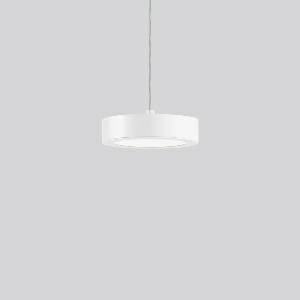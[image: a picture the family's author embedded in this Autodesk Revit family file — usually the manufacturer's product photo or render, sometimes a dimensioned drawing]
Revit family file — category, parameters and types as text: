
# Revit family: toledo_flat_round_p_901685_002_1_76_fe41
name_source: partatom
category: Lighting Fixtures
units: mm (PartAtom-declared; Revit-internal decimal feet)

## family parameters
Cut with Voids When Loaded = No
Host = Face
Light Source = No
Part Type = Normal
Room Calculation Point = No
Round Connector Dimension = Use Diameter
Shared = No

## types (1)
- TOLEDO FLAT round P (1 x LED Modul 840, 1800 lm, 4000)
    Apparent Load = 17 VA
    CIE Flux Codes = 48 79 96 100 100
    Color Rendering = 80
    Color Temperature = 4000
    Default Elevation = 1800 mm  [stored 5.90551 ft]
    Description = Series: TOLEDO FLAT
Flat cylindrical pendant luminaire. Cylinder housing sheet steel, powder-coated. Housing: die cast aluminium and sheet steel, powder-coated. Bezel ring: die-cast aluminium, powder-coated. Canopy: sheet steel, powder-coated. Lightguide and diffuser made of non-yellowing plastic (PMMA) opal matt. Suitable for pendant. Transparent suspension cable 2 m, can be shortened. Mounting rings for retrofitting a fabric lampshade available as accessory. 
Colour: white
Diameter: 257 mm
Height: 88.8 mm
Suspension length: 2000 mm
Lamp: LED
Socket: without socket
Colour temperature: 4000K
Colour rendering index (CRI): 80
System power: 17 W
Rated luminous flux: 1800 lm
Luminous efficiency: 106 lm/W
Control gear: Converter, dimmable, DALI
Protection class: I
Type of protection: IP 20
    Height = 89 mm
    Lamp = 1 x LED Modul 840
    Lamp Light Flux = 1800 lm
    Lamp count = 1
    Length = 257 mm
    Lifetime = 50000 h
    Luminous efficacy = 106 lm/W
    Manufacturer = RZB
    ModVariant = No
    Model = 901685.002.1.76
    Mounting Place = Ceiling
    Mounting Type = Pendant
    Number of Poles = 1
    OnlyDefault = Yes
    Power Factor = 1
    Product Name = TOLEDO FLAT round P
    Product group = Pendant luminaires
    ProductGroupID = 902
    Protection Class = Protection class I
    Protection Degree = IP 20
    RLX_Detail_Level = 1
    RLX_Emergency_Light_Flux = 0 lm
    RLX_Emergency_Type = 0
    RLX_Emergency_Type_DB = No
    RlxData = <blob elided: 70029 chars, md5=42469f01>
    Socket = socket
    Standby Power = 0 W
    System Light Flux = 1800 lm
    System Power = 17 W
    Type Comments = Product without accessories
    Type Image = 901685.002.jpg
    URL = http://relux.com
    VarID = ---
    Voltage = 230 V
    Voltage Range = 220-240 V
    Weight = 0.00 kg
    Width = 0 mm  [stored 0 ft]

note: [stored X ft] marks values corroborated as IEEE doubles in the binary element streams (Revit-internal decimal feet)

## geometry (parser evidence)
native form markers: Blend x4, Sweep x11
no freeform markers — native parametric forms only
